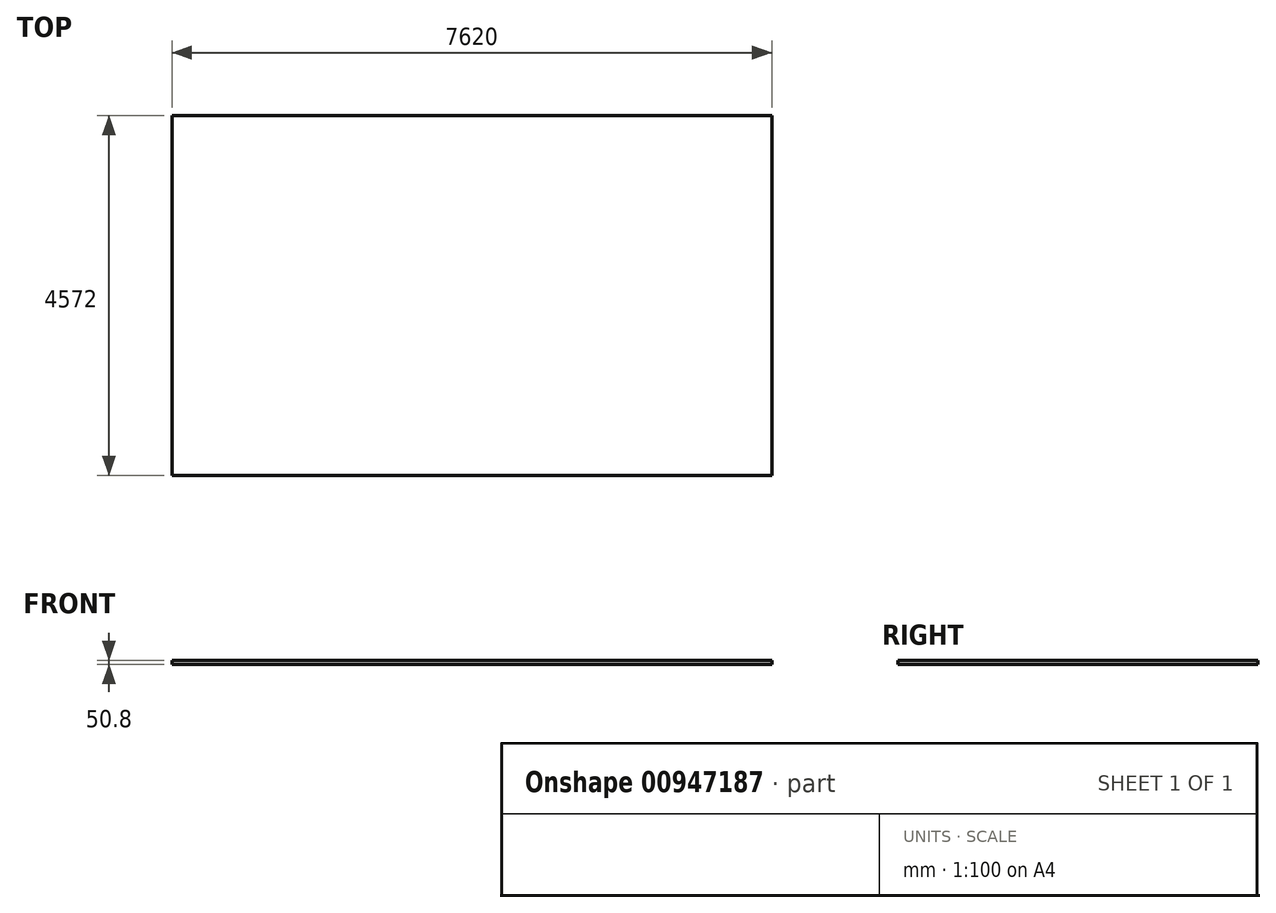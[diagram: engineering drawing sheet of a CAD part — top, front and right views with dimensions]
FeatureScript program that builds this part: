
annotation { "Feature Type Name" : "Feature", "Feature Type Description" : "" }
export const myFeature = defineFeature(function(context is Context, id is Id, definition is map)
    precondition{}
    {
        {
            var Q0;
            Q0=qCreatedBy(makeId("Top.planeOp"),FACE);
            var sketch = newSketch(context, id + "F0", { "sketchPlane" : qUnion([Q0])});
            skLineSegment(sketch, "E0.bottom", {"start": v(0, 0) * mm, "end": v(7620, 0) * mm});
            skLineSegment(sketch, "E0.top", {"start": v(0, 4572) * mm, "end": v(7620, 4572) * mm});
            skLineSegment(sketch, "E0.left", {"start": v(0, 0) * mm, "end": v(0, 4572) * mm});
            skLineSegment(sketch, "E0.right", {"start": v(7620, 0) * mm, "end": v(7620, 4572) * mm});
            skSolve(sketch);
        }
        {
            var Q0;
            Q0 = qSketchRegion(id + "F0", true);
            extrude(context, id + "F1", {"entities" : qUnion([Q0]), "depth" : 50.8 * mm, "offsetDistance" : 25.4 * mm});
        }
    });
